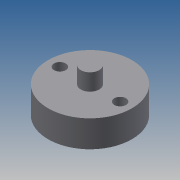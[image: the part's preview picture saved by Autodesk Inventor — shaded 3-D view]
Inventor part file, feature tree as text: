
AUTODESK INVENTOR PART (.ipt)
format: ipt  version: 2013 (Build 170138000, 138)  size: 113,664 bytes
history: native  units: mm
features: extrude x4, sketch x4, chamfer x1
ambient origin geometry x8: Origin, YZ Plane, XZ Plane, XY Plane, X Axis, Y Axis, Z Axis, Center Point
bodies: Solid1 (feature_tree)
feature tree (9):
  extrude  "Extrusion1"  Depth=8.0mm TaperAngle=0.0deg
  extrude  "Extrusion2"  Depth=5.0mm TaperAngle=0.0deg
  extrude  "Extrusion3"  Depth=7.5mm
  extrude  "Extrusion4"  Depth=5.0mm TaperAngle=0.0deg
  chamfer  "Chamfer2"  Distance=5.5mm
  sketch  "Sketch1"  dims[d0=25.0mm d2=8.0mm d3=0.0mm]
  sketch  "Sketch2"  dims[d4=5.5mm d6=5.0mm d7=0.0mm]
  sketch  "Sketch3"  dims[d8=7.5mm d9=7.5mm]
  sketch  "Sketch4"  dims[d10=3.5mm d11=5.0mm d12=0.0mm d13=5.5mm d14=4.0mm d15=0.0mm d19=2.0mm d20=2.0mm d21=45.0deg]
